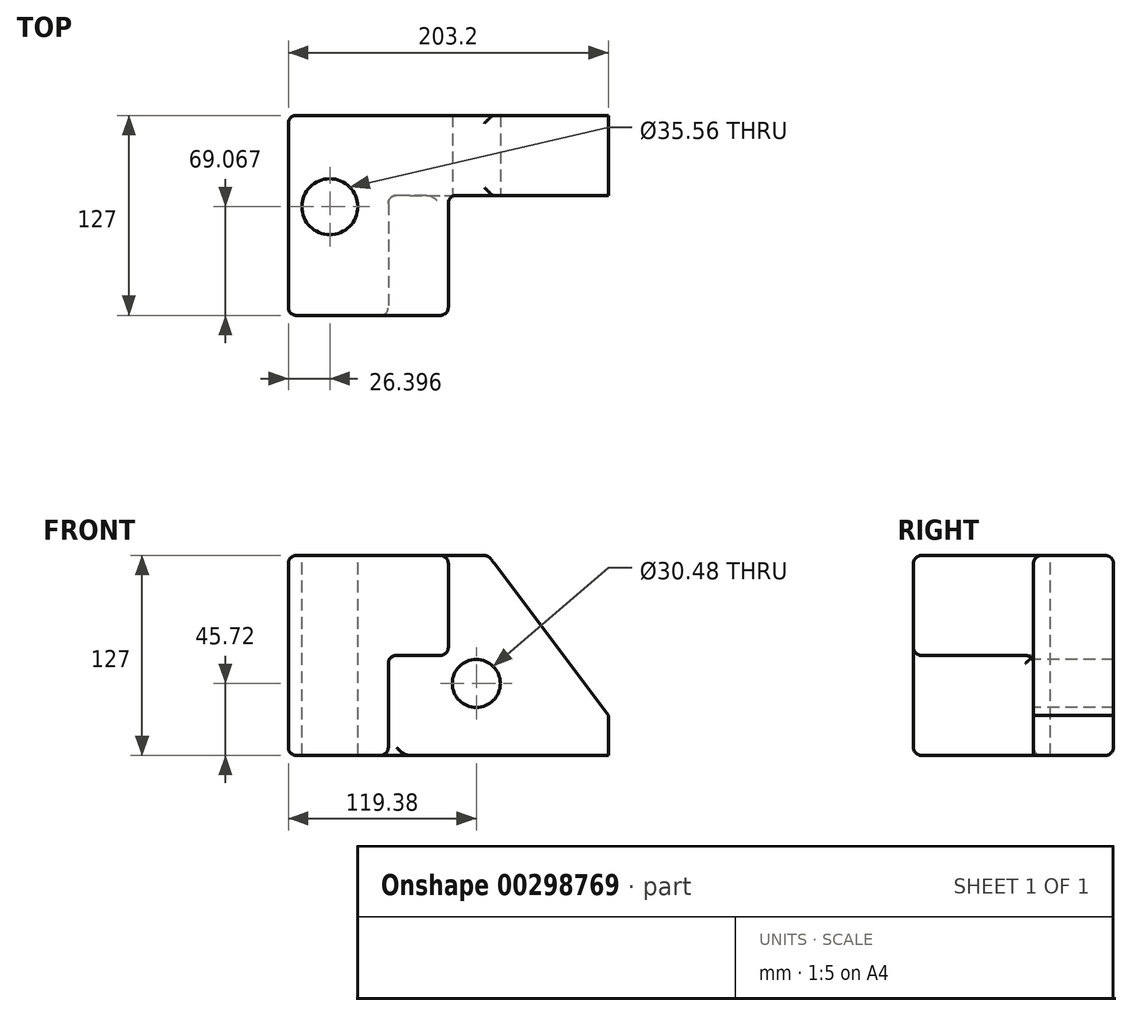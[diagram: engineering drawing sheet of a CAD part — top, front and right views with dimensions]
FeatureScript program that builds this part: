
annotation { "Feature Type Name" : "Feature", "Feature Type Description" : "" }
export const myFeature = defineFeature(function(context is Context, id is Id, definition is map)
    precondition{}
    {
        {
            var Q0;
            Q0=qCreatedBy(makeId("Front.planeOp"),FACE);
            var sketch = newSketch(context, id + "F0", { "sketchPlane" : qUnion([Q0])});
            skLineSegment(sketch, "E0.bottom", {"start": v(-101.6, 63.5) * mm, "end": v(101.6, 63.5) * mm});
            skLineSegment(sketch, "E0.top", {"start": v(-101.6, -63.5) * mm, "end": v(101.6, -63.5) * mm});
            skLineSegment(sketch, "E0.left", {"start": v(-101.6, 63.5) * mm, "end": v(-101.6, -63.5) * mm});
            skLineSegment(sketch, "E0.right", {"start": v(101.6, 63.5) * mm, "end": v(101.6, -63.5) * mm});
            skPoint(sketch, "E0.middle", {"position": v(0, 0) * mm});
            skSolve(sketch);
        }
        {
            var Q0;
            Q0=makeQuery(id+"F0.imprint","IMPRINT",FACE,{"disambiguationData":[TD([[makeQuery(id+"F0.imprint","IMPRINT",EDGE,{"derivedFrom":sQuery(id+"F0.wireOp",EDGE,"E0.bottom")}),-1.0]])]});
            extrude(context, id + "F1", {"entities" : qUnion([Q0]), "depth" : 127 * mm});
        }
        {
            var Q0;
            Q0=makeQuery(id+"F1.opExtrude","CAP_FACE",FACE,{"disambiguationData":[OSD([sQuery(id+"F0.wireOp",EDGE,"E0.bottom"),sQuery(id+"F0.wireOp",EDGE,"E0.top"),sQuery(id+"F0.wireOp",EDGE,"E0.left"),sQuery(id+"F0.wireOp",EDGE,"E0.right")])],"isStart":false});
            var sketch = newSketch(context, id + "F2", { "sketchPlane" : qUnion([Q0])});
            skLineSegment(sketch, "E1", {"start": v(-101.6, -63.5) * mm, "end": v(-101.6, 63.5) * mm});
            skLineSegment(sketch, "E2", {"start": v(-101.6, 63.5) * mm, "end": v(0, 63.5) * mm});
            skLineSegment(sketch, "E3", {"start": v(0, 63.5) * mm, "end": v(0, 0) * mm});
            skLineSegment(sketch, "E4", {"start": v(0, 0) * mm, "end": v(-38.1, 0) * mm});
            skLineSegment(sketch, "E5", {"start": v(-38.1, 0) * mm, "end": v(-38.1, -63.5) * mm});
            skLineSegment(sketch, "E6", {"start": v(-38.1, -63.5) * mm, "end": v(-101.6, -63.5) * mm});
            skSolve(sketch);
        }
        {
            var Q0;
            {var subQ2=sQuery(id+"F2.wireOp",EDGE,"E3");Q0=makeQuery(id+"F2.imprint","IMPRINT",FACE,{"disambiguationData":[TD([[makeQuery(id+"F2.imprint","IMPRINT",EDGE,{"derivedFrom":subQ2}),1.0]])]});}
            extrude(context, id + "F3", {"entities" : qUnion([Q0]), "operationType" : NewBodyOperationType.REMOVE, "oppositeDirection" : true, "depth" : 76.2 * mm});
        }
        {
            var Q0;
            Q0=makeQuery(id+"F1.opExtrude","SWEPT_EDGE",EDGE,{"disambiguationData":[OSD([sQuery(id+"F0.wireOp",EDGE,"E0.bottom"),sQuery(id+"F0.wireOp",EDGE,"E0.right")])]});
            chamfer(context, id + "F4", {"entities" : qUnion([Q0]), "chamferType" : ChamferType.TWO_OFFSETS, "width1" : 76.2 * mm, "oppositeDirection" : false, "width2" : 101.6 * mm, "tangentPropagation" : true});
        }
        {
            var Q0;
            Q0=makeQuery(id+"F1.opExtrude","CAP_FACE",FACE,{"disambiguationData":[OSD([sQuery(id+"F0.wireOp",EDGE,"E0.bottom"),sQuery(id+"F0.wireOp",EDGE,"E0.top"),sQuery(id+"F0.wireOp",EDGE,"E0.left"),sQuery(id+"F0.wireOp",EDGE,"E0.right")])],"isStart":false});
            var Q1;
            Q1=makeQuery(id+"F3.boolean.opBoolean","COPY",FACE,{"derivedFrom":makeQuery(id+"F3.opExtrude","SWEPT_FACE",FACE,{"disambiguationData":[OSD([sQuery(id+"F2.wireOp",EDGE,"E3")])]})});
            var Q2;
            Q2=makeQuery(id+"F3.boolean.opBoolean","COPY",FACE,{"derivedFrom":makeQuery(id+"F3.opExtrude","SWEPT_FACE",FACE,{"disambiguationData":[OSD([sQuery(id+"F2.wireOp",EDGE,"E5")])]})});
            var Q3;
            Q3=makeQuery(id+"F1.opExtrude","SWEPT_FACE",FACE,{"disambiguationData":[OSD([sQuery(id+"F0.wireOp",EDGE,"E0.bottom")])]});
            var Q4;
            Q4=makeQuery(id+"F1.opExtrude","SWEPT_FACE",FACE,{"disambiguationData":[OSD([sQuery(id+"F0.wireOp",EDGE,"E0.left")])]});
            var Q5;
            Q5=makeQuery(id+"F1.opExtrude","SWEPT_EDGE",EDGE,{"disambiguationData":[OSD([sQuery(id+"F0.wireOp",EDGE,"E0.top"),sQuery(id+"F0.wireOp",EDGE,"E0.left")])]});
            var Q6;
            Q6=makeQuery(id+"F1.opExtrude","CAP_EDGE",EDGE,{"disambiguationData":[OSD([sQuery(id+"F0.wireOp",EDGE,"E0.top")])],"isStart":true});
            fillet(context, id + "F5", {"entities" : qUnion([Q0, Q1, Q2, Q3, Q4, Q5, Q6]), "radius" : 5.08 * mm, "tangentPropagation" : true, "allowEdgeOverflow" : false});
        }
        {
            var Q0;
            Q0=makeQuery(id+"F3.boolean.opBoolean","COPY",FACE,{"derivedFrom":makeQuery(id+"F3.opExtrude","CAP_FACE",FACE,{"disambiguationData":[OSD([sQuery(id+"F0.wireOp",EDGE,"E0.bottom"),sQuery(id+"F0.wireOp",EDGE,"E0.top"),sQuery(id+"F0.wireOp",EDGE,"E0.right"),sQuery(id+"F2.wireOp",EDGE,"E3"),sQuery(id+"F2.wireOp",EDGE,"E4"),sQuery(id+"F2.wireOp",EDGE,"E5")])],"isStart":false})});
            var sketch = newSketch(context, id + "F6", { "sketchPlane" : qUnion([Q0])});
            skCircle(sketch, "E7", {"center": v(17.78, -17.78) * mm, "radius": 15.24 * mm});
            skSolve(sketch);
        }
        {
            var Q0;
            Q0=makeQuery(id+"F6.imprint","IMPRINT",FACE,{"disambiguationData":[TD([[makeQuery(id+"F6.imprint","IMPRINT",EDGE,{"derivedFrom":sQuery(id+"F6.wireOp",EDGE,"E7")}),1.0]])]});
            extrude(context, id + "F7", {"entities" : qUnion([Q0]), "operationType" : NewBodyOperationType.REMOVE, "endBound" : BoundingType.THROUGH_ALL, "oppositeDirection" : true, "depth" : 25.4 * mm});
        }
        {
            var Q0;
            Q0=makeQuery(id+"F1.opExtrude","SWEPT_FACE",FACE,{"disambiguationData":[OSD([sQuery(id+"F0.wireOp",EDGE,"E0.bottom")])]});
            var sketch = newSketch(context, id + "F8", { "sketchPlane" : qUnion([Q0])});
            skCircle(sketch, "E8", {"center": v(-75.2, -57.93) * mm, "radius": 17.78 * mm});
            skSolve(sketch);
        }
        {
            var Q0;
            Q0=makeQuery(id+"F8.imprint","IMPRINT",FACE,{"disambiguationData":[TD([[makeQuery(id+"F8.imprint","IMPRINT",EDGE,{"derivedFrom":sQuery(id+"F8.wireOp",EDGE,"E8")}),1.0]])]});
            extrude(context, id + "F9", {"entities" : qUnion([Q0]), "operationType" : NewBodyOperationType.REMOVE, "endBound" : BoundingType.THROUGH_ALL, "oppositeDirection" : true, "depth" : 25.4 * mm});
        }
    });
